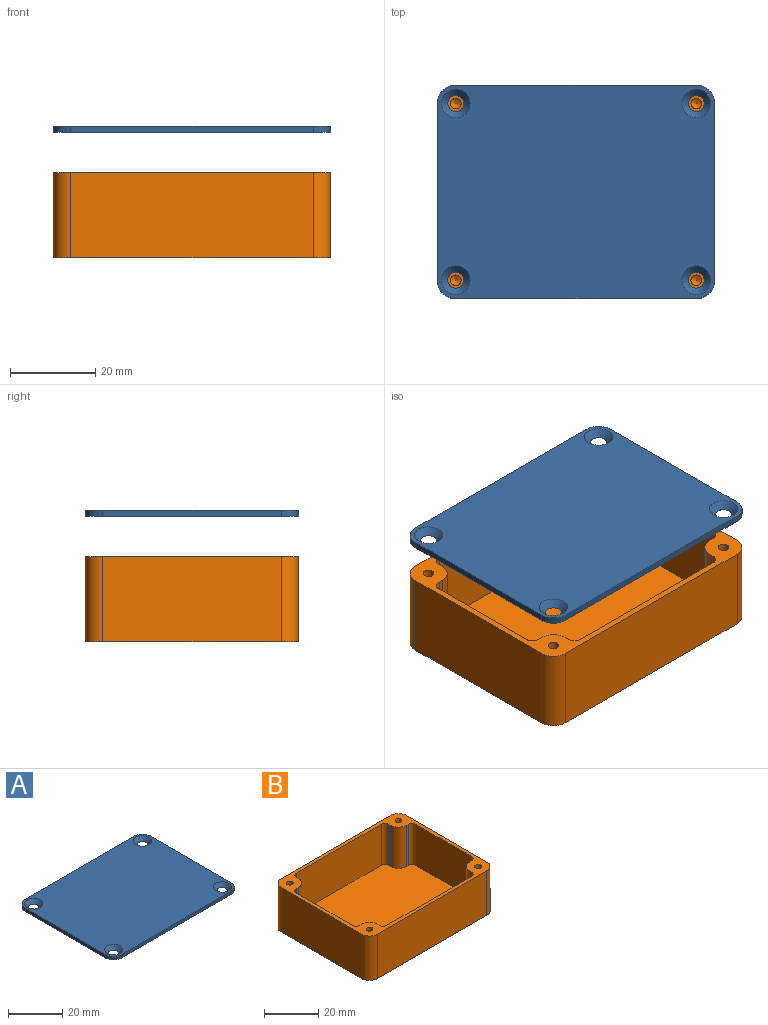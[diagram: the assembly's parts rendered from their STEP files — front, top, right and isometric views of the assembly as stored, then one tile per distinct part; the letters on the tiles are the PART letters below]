
ASSEMBLY  parts=2 mates=1
PART A: 14 faces, bbox 65x50x1.5 mm
  f0: plane 57x1.5mm, normal (0,1,0), area 85.5mm2, adj f4,f5,f10,f13
  f1: plane 42x1.5mm, normal (-1,0,0), area 63mm2, adj f4,f5,f10,f11
  f2: plane 57x1.5mm, normal (0,-1,0), area 85.5mm2, adj f4,f5,f11,f12
  f3: plane 42x1.5mm, normal (1,0,0), area 63mm2, adj f4,f5,f12,f13
  f4: plane 65x50mm, normal (0,0,1), area 3094.4mm2, adj f0,f1,f2,f3,f6,f7,f8,f9
  f5: plane 65x50mm, normal (0,0,-1), area 3192.8mm2, adj f0,f1,f2,f3,f6,f7,f8,f9
  f6: cone r=1.7mm half-angle=45deg, axis (0,0,1), area 34.8mm2, adj f4,f5
  f7: cone r=1.7mm half-angle=45deg, axis (0,0,1), area 34.8mm2, adj f4,f5
  f8: cone r=1.7mm half-angle=45deg, axis (0,0,1), area 34.8mm2, adj f4,f5
  f9: cone r=1.7mm half-angle=45deg, axis (0,0,1), area 34.8mm2, adj f4,f5
  f10: cylinder r=4mm len=4mm, axis (0,0,1), area 9.4mm2, adj f0,f1,f4,f5
  f11: cylinder r=4mm len=4mm, axis (0,0,-1), area 9.4mm2, adj f1,f2,f4,f5
  f12: cylinder r=4mm len=4mm, axis (0,0,1), area 9.4mm2, adj f2,f3,f4,f5
  f13: cylinder r=4mm len=4mm, axis (0,0,-1), area 9.4mm2, adj f0,f3,f4,f5
PART B: 43 faces, bbox 65x50x20 mm
  f0: plane 62x47mm, normal (0,0,1), area 2724.9mm2, adj f1,f2,f3,f4,f11,f12,f13,f14
  f1: plane 44x18.5mm, normal (0,1,0), area 814mm2, adj f0,f5,f35,f37
  f2: plane 29x18.5mm, normal (-1,0,0), area 536.5mm2, adj f0,f5,f38,f39
  f3: plane 44x18.5mm, normal (0,-1,0), area 814mm2, adj f0,f5,f40,f41
  f4: plane 29x18.5mm, normal (1,0,0), area 536.5mm2, adj f0,f5,f36,f42
  f5: plane 65x50mm, normal (0,0,1), area 491.8mm2, adj f1,f2,f3,f4,f6,f7,f8,f9
  f6: plane 57x20mm, normal (0,1,0), area 1140mm2, adj f5,f10,f31,f34
  f7: plane 42x20mm, normal (-1,0,0), area 840mm2, adj f5,f10,f31,f32
  f8: plane 57x20mm, normal (0,-1,0), area 1140mm2, adj f5,f10,f32,f33
  f9: plane 42x20mm, normal (1,0,0), area 840mm2, adj f5,f10,f33,f34
  f10: plane 65x50mm, normal (0,0,-1), area 3236.3mm2, adj f6,f7,f8,f9,f31,f32,f33,f34
  f11: plane 18.5x1mm, normal (0,-1,0), area 18.5mm2, adj f0,f5,f30,f42
  f12: plane 18.5x1mm, normal (1,0,0), area 18.5mm2, adj f0,f5,f30,f41
  f13: plane 18.5x1mm, normal (0,1,0), area 18.5mm2, adj f0,f5,f27,f36
  f14: plane 18.5x1mm, normal (1,0,0), area 18.5mm2, adj f0,f5,f27,f35
  f15: plane 18.5x1mm, normal (0,-1,0), area 18.5mm2, adj f0,f5,f29,f39
  f16: plane 18.5x1mm, normal (-1,0,0), area 18.5mm2, adj f0,f5,f29,f40
  f17: plane 18.5x1mm, normal (0,1,0), area 18.5mm2, adj f0,f5,f28,f38
  f18: plane 18.5x1mm, normal (-1,0,0), area 18.5mm2, adj f0,f5,f28,f37
  f19: cone r=0mm half-angle=59deg, axis (0,0,1), area 5.7mm2, adj f20
  f20: cylinder r=1.25mm len=13.5mm, axis (0,0,1), area 106mm2, adj f5,f19
  f21: cone r=0mm half-angle=59deg, axis (0,0,1), area 5.7mm2, adj f22
  f22: cylinder r=1.25mm len=13.5mm, axis (0,0,1), area 106mm2, adj f5,f21
  f23: cone r=0mm half-angle=59deg, axis (0,0,1), area 5.7mm2, adj f24
  f24: cylinder r=1.25mm len=13.5mm, axis (0,0,1), area 106mm2, adj f5,f23
  f25: cone r=0mm half-angle=59deg, axis (0,0,1), area 5.7mm2, adj f26
  f26: cylinder r=1.25mm len=13.5mm, axis (0,0,1), area 106mm2, adj f5,f25
  f27: cylinder r=4mm len=18.5mm, axis (0,0,1), area 116.2mm2, adj f0,f5,f13,f14
  f28: cylinder r=4mm len=18.5mm, axis (0,0,1), area 116.2mm2, adj f0,f5,f17,f18
  f29: cylinder r=4mm len=18.5mm, axis (0,0,1), area 116.2mm2, adj f0,f5,f15,f16
  f30: cylinder r=4mm len=18.5mm, axis (0,0,1), area 116.2mm2, adj f0,f5,f11,f12
  f31: cylinder r=4mm len=20mm, axis (0,0,1), area 125.7mm2, adj f5,f6,f7,f10
  f32: cylinder r=4mm len=20mm, axis (0,0,-1), area 125.7mm2, adj f5,f7,f8,f10
  f33: cylinder r=4mm len=20mm, axis (0,0,1), area 125.7mm2, adj f5,f8,f9,f10
  f34: cylinder r=4mm len=20mm, axis (0,0,-1), area 125.7mm2, adj f5,f6,f9,f10
  f35: cylinder r=2mm len=18.5mm, axis (0,0,-1), area 58.1mm2, adj f0,f1,f5,f14
  f36: cylinder r=2mm len=18.5mm, axis (0,0,1), area 58.1mm2, adj f0,f4,f5,f13
  f37: cylinder r=2mm len=18.5mm, axis (0,0,1), area 58.1mm2, adj f0,f1,f5,f18
  f38: cylinder r=2mm len=18.5mm, axis (0,0,1), area 58.1mm2, adj f0,f2,f5,f17
  f39: cylinder r=2mm len=18.5mm, axis (0,0,-1), area 58.1mm2, adj f0,f2,f5,f15
  f40: cylinder r=2mm len=18.5mm, axis (0,0,1), area 58.1mm2, adj f0,f3,f5,f16
  f41: cylinder r=2mm len=18.5mm, axis (0,0,-1), area 58.1mm2, adj f0,f3,f5,f12
  f42: cylinder r=2mm len=18.5mm, axis (0,0,-1), area 58.1mm2, adj f0,f4,f5,f11
PLACE A t=(2.23,24.29,32.64)mm
PLACE B t=(-3.01,-53.94,3.14)mm
MATE slider B.f25 <-> A.f8  axis (0,0,1) through (25.24,-74.69,23.14)mm
